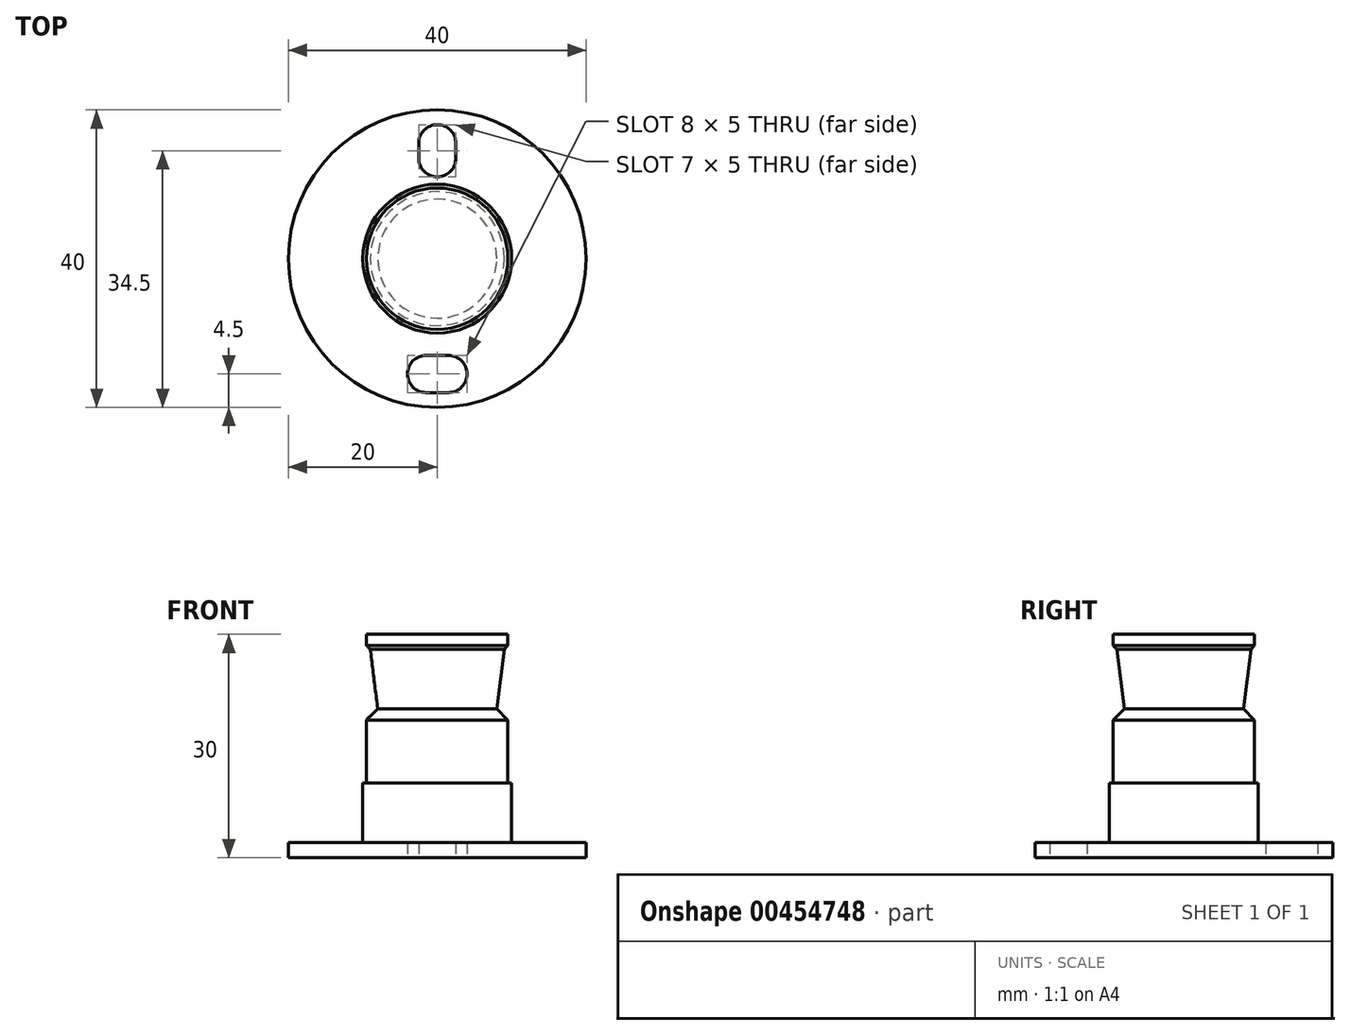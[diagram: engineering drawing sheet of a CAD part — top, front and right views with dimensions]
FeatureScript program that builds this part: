
annotation { "Feature Type Name" : "Feature", "Feature Type Description" : "" }
export const myFeature = defineFeature(function(context is Context, id is Id, definition is map)
    precondition{}
    {
        {
            var Q0;
            Q0=qCreatedBy(makeId("Top.planeOp"),FACE);
            var sketch = newSketch(context, id + "F0", { "sketchPlane" : qUnion([Q0])});
            skCircle(sketch, "E0", {"center": v(0, 0) * mm, "radius": 20 * mm});
            skLineSegment(sketch, "E1.bottom", {"start": v(1.5, -13) * mm, "end": v(-1.5, -13) * mm});
            skLineSegment(sketch, "E1.top", {"start": v(1.5, -18) * mm, "end": v(-1.5, -18) * mm});
            skPoint(sketch, "E1.middle", {"position": v(0, -15.5) * mm});
            skArc(sketch, "E2", {"start": v(1.5, -18) * mm, "mid": v(4, -15.5) * mm, "end": v(1.5, -13) * mm});
            skArc(sketch, "E3", {"start": v(-1.5, -13) * mm, "mid": v(-4, -15.5) * mm, "end": v(-1.5, -18) * mm});
            skLineSegment(sketch, "E4.left", {"start": v(-2.5, 13.5) * mm, "end": v(-2.5, 15.5) * mm});
            skLineSegment(sketch, "E4.right", {"start": v(2.5, 13.5) * mm, "end": v(2.5, 15.5) * mm});
            skPoint(sketch, "E4.middle", {"position": v(0, 14.5) * mm});
            skArc(sketch, "E5", {"start": v(-2.5, 15.5) * mm, "mid": v(0, 18) * mm, "end": v(2.5, 15.5) * mm});
            skArc(sketch, "E6", {"start": v(2.5, 13.5) * mm, "mid": v(0, 11) * mm, "end": v(-2.5, 13.5) * mm});
            skSolve(sketch);
        }
        {
            var Q0;
            Q0=makeQuery(id+"F0.imprint","IMPRINT",FACE,{"disambiguationData":[TD([[makeQuery(id+"F0.imprint","IMPRINT",EDGE,{"derivedFrom":sQuery(id+"F0.wireOp",EDGE,"E0")}),1.0]])]});
            extrude(context, id + "F1", {"entities" : qUnion([Q0]), "depth" : 2 * mm});
        }
        {
            var Q0;
            Q0=qCreatedBy(makeId("Front.planeOp"),FACE);
            var sketch = newSketch(context, id + "F2", { "sketchPlane" : qUnion([Q0])});
            skLineSegment(sketch, "E7.0", {"start": v(0, 2) * mm, "end": v(10, 2) * mm});
            skLineSegment(sketch, "E8", {"start": v(0, 2) * mm, "end": v(0, 86.01) * mm, "construction": true});
            skPoint(sketch, "E8.endSnap0", {"position": v(0, 2) * mm});
            skLineSegment(sketch, "E9", {"start": v(0, 2) * mm, "end": v(0, 30) * mm});
            skLineSegment(sketch, "E10", {"start": v(10, 10) * mm, "end": v(10, 2) * mm});
            skPoint(sketch, "E11.orphan", {"position": v(20, 2) * mm});
            skPoint(sketch, "E12.orphan", {"position": v(-20, 2) * mm});
            skLineSegment(sketch, "E13", {"start": v(10, 10) * mm, "end": v(9.5, 10) * mm});
            skLineSegment(sketch, "E14", {"start": v(9.5, 10) * mm, "end": v(9.5, 20) * mm});
            skLineSegment(sketch, "E15", {"start": v(9.5, 20) * mm, "end": v(8, 20) * mm});
            skLineSegment(sketch, "E16", {"start": v(8, 20) * mm, "end": v(9, 28) * mm});
            skLineSegment(sketch, "E17", {"start": v(9, 28) * mm, "end": v(9.5, 28) * mm});
            skLineSegment(sketch, "E18", {"start": v(9.5, 28) * mm, "end": v(9.5, 30) * mm});
            skLineSegment(sketch, "E19", {"start": v(9.5, 30) * mm, "end": v(0, 30) * mm});
            skSolve(sketch);
        }
        {
            var Q0;
            Q0=makeQuery(id+"F2.imprint","IMPRINT",FACE,{"disambiguationData":[TD([[makeQuery(id+"F2.imprint","IMPRINT",EDGE,{"derivedFrom":sQuery(id+"F2.wireOp",EDGE,"E7.0")}),1.0]])]});
            var Q1;
            Q1=sQuery(id+"F2.wireOp",EDGE,"E8");
            revolve(context, id + "F3", {"operationType" : NewBodyOperationType.ADD, "entities" : qUnion([Q0]), "axis" : qUnion([Q1]), "revolveType" : RevolveType.FULL});
        }
        {
            var Q0;
            Q0=makeQuery(id+"F3.opRevolve","SWEPT_EDGE",EDGE,{"disambiguationData":[OSD([sQuery(id+"F2.wireOp",EDGE,"E17"),sQuery(id+"F2.wireOp",EDGE,"E18")])]});
            chamfer(context, id + "F4", {"entities" : qUnion([Q0]), "width" : 0.5 * mm, "tangentPropagation" : true});
        }
        {
            var Q0;
            Q0=makeQuery(id+"F3.opRevolve","SWEPT_EDGE",EDGE,{"disambiguationData":[OSD([sQuery(id+"F2.wireOp",EDGE,"E14"),sQuery(id+"F2.wireOp",EDGE,"E15")])]});
            chamfer(context, id + "F5", {"entities" : qUnion([Q0]), "width" : 1.5 * mm, "tangentPropagation" : true});
        }
    });
